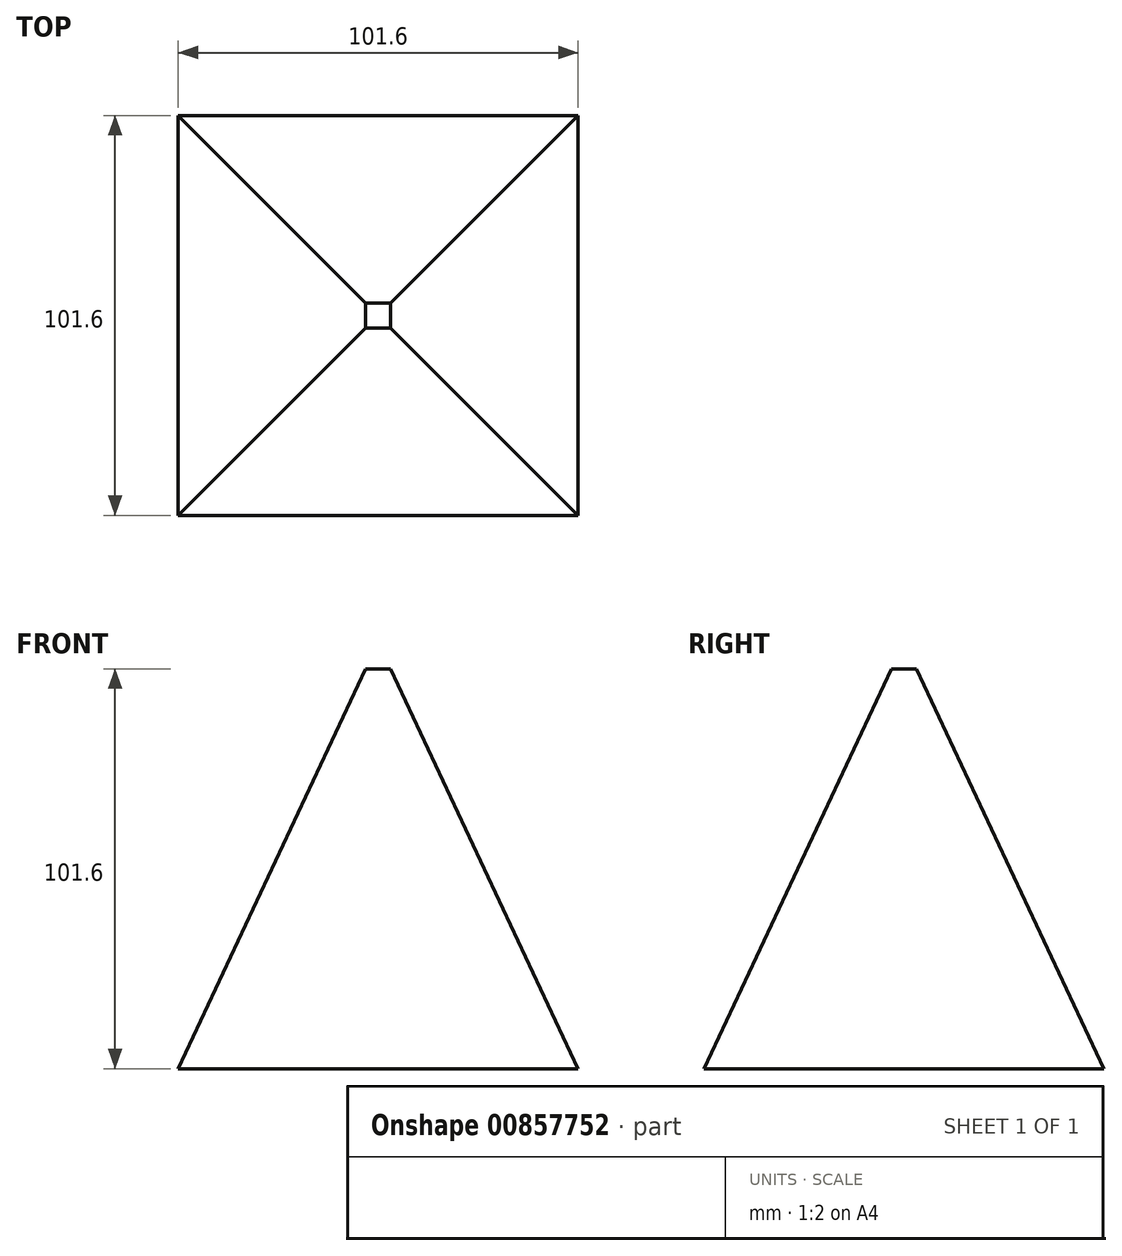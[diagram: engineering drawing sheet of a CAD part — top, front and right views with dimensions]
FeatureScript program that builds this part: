
annotation { "Feature Type Name" : "Feature", "Feature Type Description" : "" }
export const myFeature = defineFeature(function(context is Context, id is Id, definition is map)
    precondition{}
    {
        {
            var Q0;
            Q0=qCreatedBy(makeId("Top.planeOp"),FACE);
            var sketch = newSketch(context, id + "F0", { "sketchPlane" : qUnion([Q0])});
            skLineSegment(sketch, "E0.bottom", {"start": v(50.8, -50.8) * mm, "end": v(-50.8, -50.8) * mm});
            skLineSegment(sketch, "E0.top", {"start": v(50.8, 50.8) * mm, "end": v(-50.8, 50.8) * mm});
            skLineSegment(sketch, "E0.left", {"start": v(50.8, -50.8) * mm, "end": v(50.8, 50.8) * mm});
            skLineSegment(sketch, "E0.right", {"start": v(-50.8, -50.8) * mm, "end": v(-50.8, 50.8) * mm});
            skPoint(sketch, "E0.middle", {"position": v(0, 0) * mm});
            skSolve(sketch);
        }
        {
            var Q0;
            Q0=qCreatedBy(makeId("Top.planeOp"),FACE);
            cPlane(context, id + "F1", {"entities" : qUnion([Q0]), "cplaneType" : CPlaneType.OFFSET, "offset" : 101.6 * mm, "width" : 152.4 * mm, "height" : 152.4 * mm});
        }
        {
            var Q0;
            Q0=qCreatedBy(id+"F1.planeOp",FACE);
            var sketch = newSketch(context, id + "F2", { "sketchPlane" : qUnion([Q0])});
            skLineSegment(sketch, "E1.bottom", {"start": v(3.18, -3.17) * mm, "end": v(-3.17, -3.17) * mm});
            skLineSegment(sketch, "E1.top", {"start": v(3.18, 3.18) * mm, "end": v(-3.17, 3.18) * mm});
            skLineSegment(sketch, "E1.left", {"start": v(3.18, -3.17) * mm, "end": v(3.18, 3.18) * mm});
            skLineSegment(sketch, "E1.right", {"start": v(-3.17, -3.17) * mm, "end": v(-3.17, 3.18) * mm});
            skPoint(sketch, "E1.middle", {"position": v(0, 0) * mm});
            skSolve(sketch);
        }
        {
            var Q0;
            Q0=makeQuery(id+"F0.imprint","IMPRINT",FACE,{"disambiguationData":[TD([[makeQuery(id+"F0.imprint","IMPRINT",EDGE,{"derivedFrom":sQuery(id+"F0.wireOp",EDGE,"E0.bottom")}),-1.0]])]});
            var Q1;
            Q1=makeQuery(id+"F2.imprint","IMPRINT",FACE,{"disambiguationData":[TD([[makeQuery(id+"F2.imprint","IMPRINT",EDGE,{"derivedFrom":sQuery(id+"F2.wireOp",EDGE,"E1.bottom")}),-1.0]])]});
            loft(context, id + "F3", {"sheetProfilesArray" : [{ "sheetProfileEntities" : qUnion([Q0]) }, { "sheetProfileEntities" : qUnion([Q1]) }]});
        }
    });
